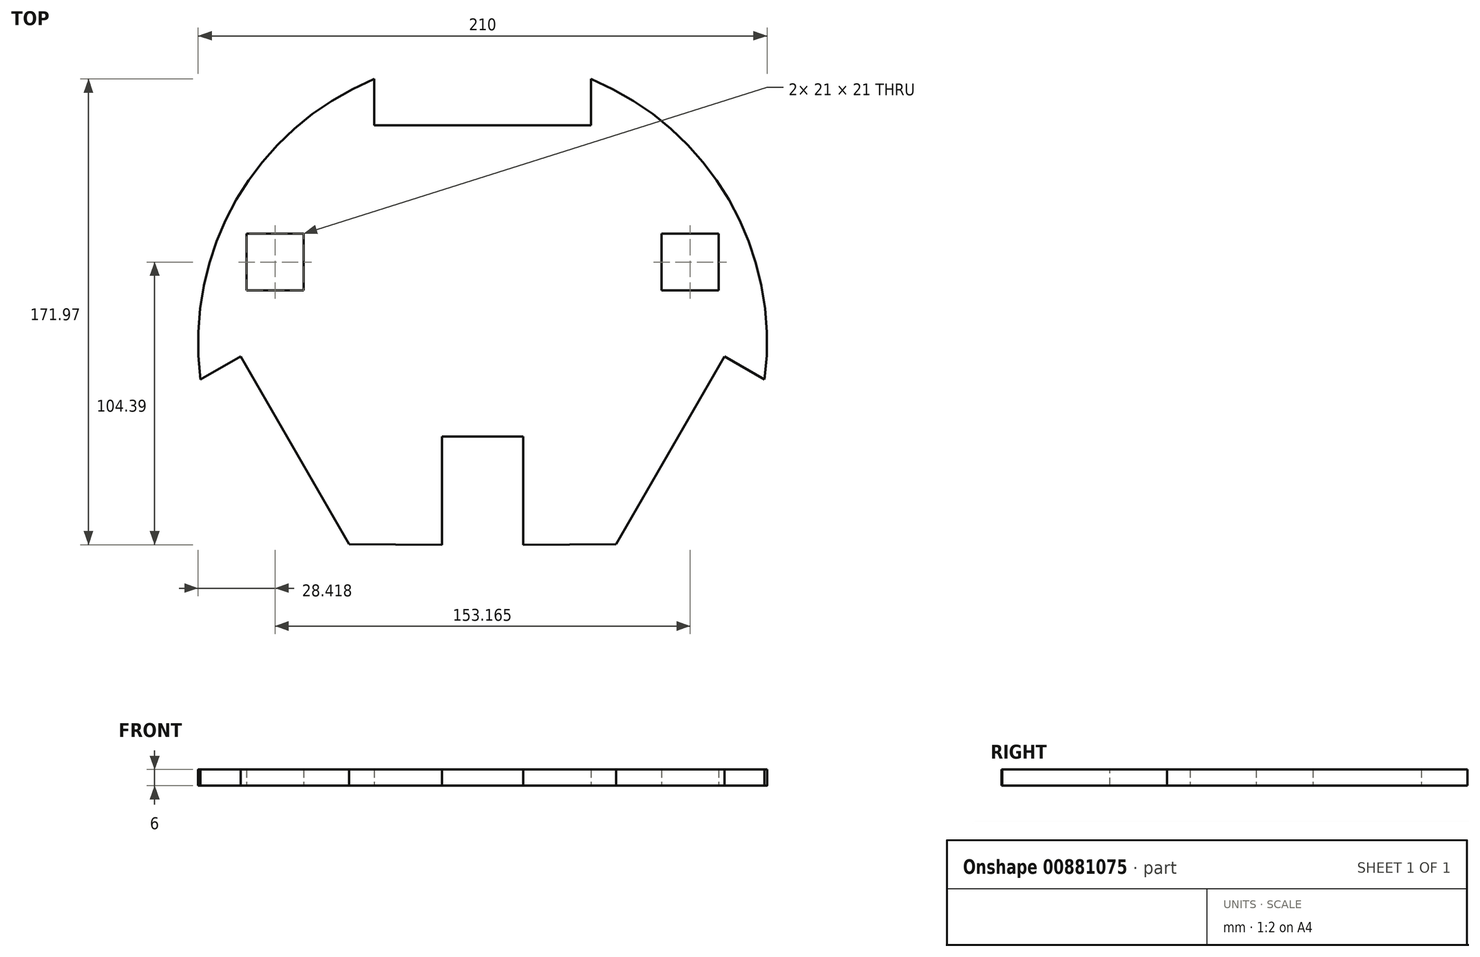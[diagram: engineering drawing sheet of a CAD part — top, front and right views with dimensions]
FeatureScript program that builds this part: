
annotation { "Feature Type Name" : "Feature", "Feature Type Description" : "" }
export const myFeature = defineFeature(function(context is Context, id is Id, definition is map)
    precondition{}
    {
        {
            var Q0;
            Q0=qCreatedBy(makeId("Top.planeOp"),FACE);
            var sketch = newSketch(context, id + "F0", { "sketchPlane" : qUnion([Q0])});
            skCircle(sketch, "E0", {"center": v(0, 0) * mm, "radius": 105 * mm});
            skLineSegment(sketch, "E1", {"start": v(0, 0) * mm, "end": v(0, -105) * mm});
            skLineSegment(sketch, "E2", {"start": v(0, 80) * mm, "end": v(40, 80) * mm});
            skLineSegment(sketch, "E3", {"start": v(40, 80) * mm, "end": v(-40, 80) * mm});
            skLineSegment(sketch, "E4", {"start": v(-40, 80) * mm, "end": v(-40, 97.08) * mm});
            skLineSegment(sketch, "E5", {"start": v(40, 80) * mm, "end": v(40, 97.08) * mm});
            skLineSegment(sketch, "E6", {"start": v(-69.28, -40) * mm, "end": v(-89.28, -5.36) * mm});
            skLineSegment(sketch, "E7", {"start": v(-89.28, -5.36) * mm, "end": v(-49.28, -74.64) * mm});
            skLineSegment(sketch, "E8", {"start": v(-49.28, -74.64) * mm, "end": v(-64.08, -83.18) * mm});
            skLineSegment(sketch, "E9", {"start": v(-89.28, -5.36) * mm, "end": v(-104.08, -13.9) * mm});
            skLineSegment(sketch, "E10", {"start": v(69.28, -40) * mm, "end": v(89.28, -5.36) * mm});
            skLineSegment(sketch, "E11", {"start": v(89.28, -5.36) * mm, "end": v(104.08, -13.9) * mm});
            skLineSegment(sketch, "E12", {"start": v(69.28, -40) * mm, "end": v(49.28, -74.64) * mm});
            skLineSegment(sketch, "E13", {"start": v(49.28, -74.64) * mm, "end": v(64.08, -83.18) * mm});
            skLineSegment(sketch, "E14", {"start": v(0, -105) * mm, "end": v(0, -75) * mm});
            skLineSegment(sketch, "E15", {"start": v(0, -75) * mm, "end": v(49.28, -74.64) * mm});
            skLineSegment(sketch, "E16", {"start": v(-49.28, -74.64) * mm, "end": v(0, -75) * mm});
            skLineSegment(sketch, "E17", {"start": v(-87.08, 40) * mm, "end": v(-87.08, 19) * mm});
            skLineSegment(sketch, "E18", {"start": v(-87.08, 19) * mm, "end": v(-66.08, 19) * mm});
            skLineSegment(sketch, "E19", {"start": v(-66.08, 19) * mm, "end": v(-66.08, 40) * mm});
            skLineSegment(sketch, "E20", {"start": v(-66.08, 40) * mm, "end": v(-87.08, 40) * mm});
            skLineSegment(sketch, "E21", {"start": v(87.08, 40) * mm, "end": v(87.08, 19) * mm});
            skLineSegment(sketch, "E22", {"start": v(87.08, 19) * mm, "end": v(66.08, 19) * mm});
            skLineSegment(sketch, "E23", {"start": v(66.08, 19) * mm, "end": v(66.08, 40) * mm});
            skLineSegment(sketch, "E24", {"start": v(66.08, 40) * mm, "end": v(87.08, 40) * mm});
            skLineSegment(sketch, "E25", {"start": v(-69.28, -40) * mm, "end": v(-30.31, -17.5) * mm});
            skLineSegment(sketch, "E26", {"start": v(69.28, -40) * mm, "end": v(30.31, -17.5) * mm});
            skLineSegment(sketch, "E27", {"start": v(30.31, -17.5) * mm, "end": v(-30.31, -17.5) * mm});
            skLineSegment(sketch, "E28", {"start": v(-30.31, 35) * mm, "end": v(-30.31, -17.5) * mm});
            skLineSegment(sketch, "E29", {"start": v(30.31, -17.5) * mm, "end": v(30.31, 35) * mm});
            skLineSegment(sketch, "E30", {"start": v(30.31, 35) * mm, "end": v(-30.31, 35) * mm});
            skLineSegment(sketch, "E31", {"start": v(-30.31, -17.5) * mm, "end": v(-56.31, 27.53) * mm});
            skLineSegment(sketch, "E32", {"start": v(-56.31, 27.53) * mm, "end": v(-95.28, 5.03) * mm});
            skLineSegment(sketch, "E33", {"start": v(-95.28, 5.03) * mm, "end": v(-89.28, -5.36) * mm});
            skLineSegment(sketch, "E34", {"start": v(30.31, -17.5) * mm, "end": v(56.31, 27.53) * mm});
            skLineSegment(sketch, "E35", {"start": v(56.31, 27.53) * mm, "end": v(95.28, 5.03) * mm});
            skLineSegment(sketch, "E36", {"start": v(95.28, 5.03) * mm, "end": v(89.28, -5.36) * mm});
            skSolve(sketch);
        }
        {
            var Q0;
            {var subQ12=sQuery(id+"F0.wireOp",EDGE,"E4");Q0=makeQuery(id+"F0.imprint","IMPRINT",FACE,{"disambiguationData":[TD([[makeQuery(id+"F0.imprint","IMPRINT",EDGE,{"derivedFrom":subQ12}),1.0]])]});}
            var Q1;
            {var subQ5=sQuery(id+"F0.wireOp",EDGE,"E25");Q1=makeQuery(id+"F0.imprint","IMPRINT",FACE,{"disambiguationData":[TD([[makeQuery(id+"F0.imprint","IMPRINT",EDGE,{"derivedFrom":subQ5}),1.0]])]});}
            var Q2;
            {var subQ1=sQuery(id+"F0.wireOp",EDGE,"E28");Q2=makeQuery(id+"F0.imprint","IMPRINT",FACE,{"disambiguationData":[TD([[makeQuery(id+"F0.imprint","IMPRINT",EDGE,{"derivedFrom":subQ1}),1.0]])]});}
            var Q3;
            Q3=makeQuery(id+"F0.imprint","IMPRINT",FACE,{"disambiguationData":[TD([[makeQuery(id+"F0.imprint","IMPRINT",EDGE,{"derivedFrom":sQuery(id+"F0.wireOp",EDGE,"E10")}),1.0]])]});
            var Q4;
            {var subQ1=sQuery(id+"F0.wireOp",EDGE,"E16");Q4=makeQuery(id+"F0.imprint","IMPRINT",FACE,{"disambiguationData":[TD([[makeQuery(id+"F0.imprint","IMPRINT",EDGE,{"derivedFrom":subQ1}),1.0]])]});}
            var Q5;
            Q5=makeQuery(id+"F0.imprint","IMPRINT",FACE,{"disambiguationData":[TD([[makeQuery(id+"F0.imprint","IMPRINT",EDGE,{"derivedFrom":sQuery(id+"F0.wireOp",EDGE,"E12")}),-1.0]])]});
            var Q6;
            Q6 = qSketchRegion(id + "FIlHWKjYNUt4j0n_0", true);
            extrude(context, id + "F1", {"entities" : qUnion([Q0, Q1, Q2, Q3, Q4, Q5, Q6]), "depth" : 6 * mm, "offsetDistance" : 25 * mm});
        }
        {
            var Q0;
            Q0=makeQuery(id+"F1.opExtrude","CAP_FACE",FACE,{"disambiguationData":[OSD([sQuery(id+"F0.wireOp",EDGE,"E0"),sQuery(id+"F0.wireOp",EDGE,"E3"),sQuery(id+"F0.wireOp",EDGE,"E4"),sQuery(id+"F0.wireOp",EDGE,"E5"),sQuery(id+"F0.wireOp",EDGE,"E7"),sQuery(id+"F0.wireOp",EDGE,"E9"),sQuery(id+"F0.wireOp",EDGE,"E10"),sQuery(id+"F0.wireOp",EDGE,"E11"),sQuery(id+"F0.wireOp",EDGE,"E12"),sQuery(id+"F0.wireOp",EDGE,"E15"),sQuery(id+"F0.wireOp",EDGE,"E16"),sQuery(id+"F0.wireOp",EDGE,"E17"),sQuery(id+"F0.wireOp",EDGE,"E18"),sQuery(id+"F0.wireOp",EDGE,"E19"),sQuery(id+"F0.wireOp",EDGE,"E20"),sQuery(id+"F0.wireOp",EDGE,"E21"),sQuery(id+"F0.wireOp",EDGE,"E22"),sQuery(id+"F0.wireOp",EDGE,"E23"),sQuery(id+"F0.wireOp",EDGE,"E24")])],"isStart":false});
            var sketch = newSketch(context, id + "F2", { "sketchPlane" : qUnion([Q0])});
            skLineSegment(sketch, "E37", {"start": v(0, -75) * mm, "end": v(15, -74.9) * mm});
            skLineSegment(sketch, "E38", {"start": v(0, -75) * mm, "end": v(-15, -74.9) * mm});
            skLineSegment(sketch, "E39", {"start": v(-15, -74.9) * mm, "end": v(-15, -34.9) * mm});
            skLineSegment(sketch, "E40", {"start": v(-15, -34.9) * mm, "end": v(15, -34.9) * mm});
            skLineSegment(sketch, "E41", {"start": v(15, -34.9) * mm, "end": v(15, -74.9) * mm});
            skSolve(sketch);
        }
        {
            var Q0;
            Q0 = qSketchRegion(id + "F2", true);
            extrude(context, id + "F3", {"entities" : qUnion([Q0]), "operationType" : NewBodyOperationType.REMOVE, "oppositeDirection" : true, "depth" : 25 * mm, "offsetDistance" : 25 * mm});
        }
    });
